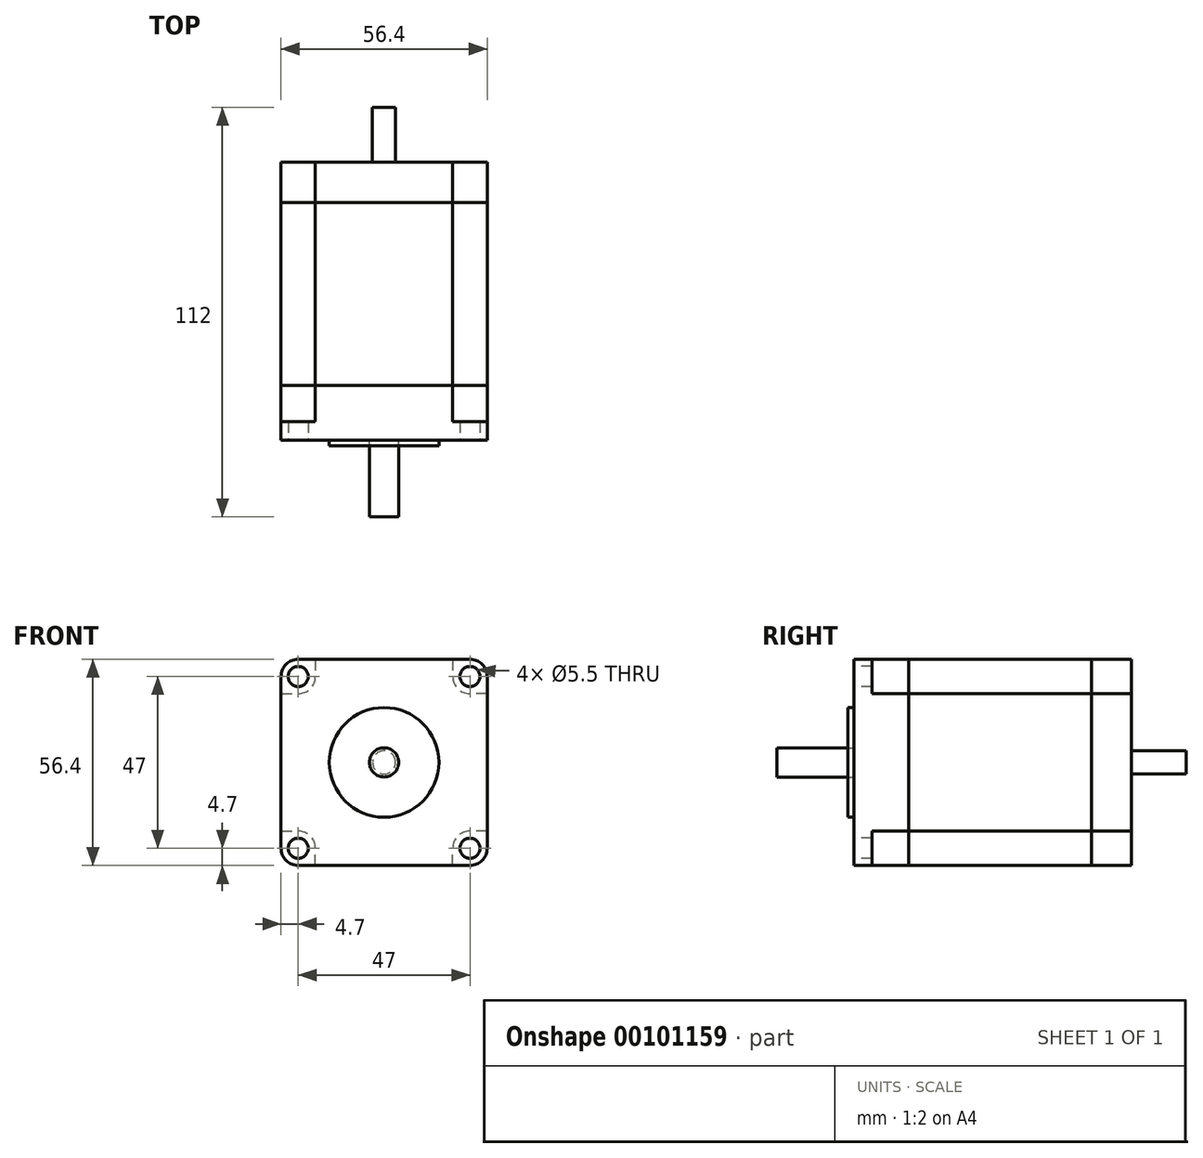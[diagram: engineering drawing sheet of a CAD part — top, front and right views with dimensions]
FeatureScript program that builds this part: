
annotation { "Feature Type Name" : "Feature", "Feature Type Description" : "" }
export const myFeature = defineFeature(function(context is Context, id is Id, definition is map)
    precondition{}
    {
        {
            var Q0;
            Q0=qCreatedBy(makeId("Front.planeOp"),FACE);
            var sketch = newSketch(context, id + "F0", { "sketchPlane" : qUnion([Q0])});
            skLineSegment(sketch, "E0.bottom", {"start": v(28.2, 28.2) * mm, "end": v(-28.2, 28.2) * mm});
            skLineSegment(sketch, "E0.top", {"start": v(28.2, -28.2) * mm, "end": v(-28.2, -28.2) * mm});
            skLineSegment(sketch, "E0.left", {"start": v(28.2, 28.2) * mm, "end": v(28.2, -28.2) * mm});
            skLineSegment(sketch, "E0.right", {"start": v(-28.2, 28.2) * mm, "end": v(-28.2, -28.2) * mm});
            skPoint(sketch, "E0.middle", {"position": v(0, 0) * mm});
            skSolve(sketch);
        }
        {
            var Q0;
            Q0=makeQuery(id+"F0.imprint","IMPRINT",FACE,{"disambiguationData":[TD([[makeQuery(id+"F0.imprint","IMPRINT",EDGE,{"derivedFrom":sQuery(id+"F0.wireOp",EDGE,"E0.bottom")}),1.0]])]});
            extrude(context, id + "F1", {"entities" : qUnion([Q0]), "oppositeDirection" : true, "depth" : 15 * mm});
        }
        {
            var Q0;
            Q0=makeQuery(id+"F1.opExtrude","CAP_FACE",FACE,{"disambiguationData":[OSD([sQuery(id+"F0.wireOp",EDGE,"E0.bottom"),sQuery(id+"F0.wireOp",EDGE,"E0.top"),sQuery(id+"F0.wireOp",EDGE,"E0.left"),sQuery(id+"F0.wireOp",EDGE,"E0.right")])],"isStart":true});
            var sketch = newSketch(context, id + "F2", { "sketchPlane" : qUnion([Q0])});
            skPoint(sketch, "E1", {"position": v(-23.5, 23.5) * mm});
            skPoint(sketch, "E2", {"position": v(23.5, 23.5) * mm});
            skPoint(sketch, "E3", {"position": v(23.5, -23.5) * mm});
            skPoint(sketch, "E4", {"position": v(-23.5, -23.5) * mm});
            skLineSegment(sketch, "E5", {"start": v(-23.5, 23.5) * mm, "end": v(-23.5, -23.5) * mm, "construction": true});
            skLineSegment(sketch, "E6", {"start": v(-23.5, -23.5) * mm, "end": v(23.5, -23.5) * mm, "construction": true});
            skLineSegment(sketch, "E7", {"start": v(23.5, -23.5) * mm, "end": v(23.5, 23.5) * mm, "construction": true});
            skLineSegment(sketch, "E8", {"start": v(-23.5, 23.5) * mm, "end": v(23.5, 23.5) * mm, "construction": true});
            skLineSegment(sketch, "E9", {"start": v(23.5, 23.5) * mm, "end": v(0, 0) * mm, "construction": true});
            skLineSegment(sketch, "E10", {"start": v(0, 0) * mm, "end": v(-23.5, -23.5) * mm, "construction": true});
            skLineSegment(sketch, "E11", {"start": v(23.5, -23.5) * mm, "end": v(0, 0) * mm, "construction": true});
            skLineSegment(sketch, "E12", {"start": v(-23.5, 23.5) * mm, "end": v(0, 0) * mm, "construction": true});
            skSolve(sketch);
        }
        {
            var Q0;
            Q0=sQuery(id+"F2.wireOp",VERTEX,"E4");
            var Q1;
            Q1=sQuery(id+"F2.wireOp",VERTEX,"E1");
            var Q2;
            Q2=sQuery(id+"F2.wireOp",VERTEX,"E2");
            var Q3;
            Q3=sQuery(id+"F2.wireOp",VERTEX,"E3");
            var Q4;
            Q4=makeQuery(id+"F1.opExtrude","SWEPT_BODY",BODY,{"disambiguationData":[OSD([sQuery(id+"F0.wireOp",EDGE,"E0.bottom"),sQuery(id+"F0.wireOp",EDGE,"E0.top"),sQuery(id+"F0.wireOp",EDGE,"E0.left"),sQuery(id+"F0.wireOp",EDGE,"E0.right")])]});
            hole(context, id + "F3", {"style" : HoleStyle.SIMPLE, "endStyle" : HoleEndStyle.THROUGH, "standardTappedOrClearance" : lookupTablePath({ "standard" : "ISO", "fit" : "Normal", "size" : "M5", "type" : "Clearance" }), "standardBlindInLast" : lookupTablePath({ "fit" : "Standard", "standard" : "ISO", "size" : "M5", "type" : "Clearance" }), "holeDiameter" : 5.5 * mm, "locations" : qUnion([Q0, Q1, Q2, Q3]), "scope" : qUnion([Q4]), "isTappedThrough" : true});
        }
        {
            var Q0;
            Q0=makeQuery(id+"F1.opExtrude","CAP_FACE",FACE,{"disambiguationData":[OSD([sQuery(id+"F0.wireOp",EDGE,"E0.bottom"),sQuery(id+"F0.wireOp",EDGE,"E0.top"),sQuery(id+"F0.wireOp",EDGE,"E0.left"),sQuery(id+"F0.wireOp",EDGE,"E0.right")])],"isStart":false});
            var sketch = newSketch(context, id + "F4", { "sketchPlane" : qUnion([Q0])});
            skLineSegment(sketch, "E13.bottom", {"start": v(28.2, 28.2) * mm, "end": v(18.8, 28.2) * mm});
            skLineSegment(sketch, "E13.top", {"start": v(28.2, 18.8) * mm, "end": v(23.5, 18.8) * mm});
            skLineSegment(sketch, "E13.left", {"start": v(28.2, 28.2) * mm, "end": v(28.2, 18.8) * mm});
            skLineSegment(sketch, "E13.right", {"start": v(18.8, 28.2) * mm, "end": v(18.8, 23.5) * mm});
            skLineSegment(sketch, "E14", {"start": v(23.5, 28.2) * mm, "end": v(23.5, 26.25) * mm, "construction": true});
            skLineSegment(sketch, "E15", {"start": v(23.5, 20.75) * mm, "end": v(23.5, 18.8) * mm, "construction": true});
            skLineSegment(sketch, "E16", {"start": v(28.2, 23.5) * mm, "end": v(26.25, 23.5) * mm, "construction": true});
            skLineSegment(sketch, "E17", {"start": v(18.8, 23.5) * mm, "end": v(20.75, 23.5) * mm, "construction": true});
            skPoint(sketch, "E18.center.orphan", {"position": v(23.5, 23.5) * mm});
            skPoint(sketch, "E19.visualSharp", {"position": v(18.8, 18.8) * mm});
            skArc(sketch, "E19.filletArc", {"start": v(18.8, 23.5) * mm, "mid": v(20.18, 20.18) * mm, "end": v(23.5, 18.8) * mm});
            skLineSegment(sketch, "E20", {"start": v(28.2, 0) * mm, "end": v(-28.2, 0) * mm, "construction": true});
            skLineSegment(sketch, "E21", {"start": v(0, 28.2) * mm, "end": v(0, -28.2) * mm, "construction": true});
            skLineSegment(sketch, "E22.MirrorCS", {"start": v(28.2, -18.8) * mm, "end": v(23.5, -18.8) * mm});
            skArc(sketch, "E23.MirrorCS", {"start": v(18.8, -23.5) * mm, "mid": v(20.18, -20.18) * mm, "end": v(23.5, -18.8) * mm});
            skLineSegment(sketch, "E24.MirrorCS", {"start": v(18.8, -28.2) * mm, "end": v(18.8, -23.5) * mm});
            skLineSegment(sketch, "E25.MirrorCS", {"start": v(28.2, -28.2) * mm, "end": v(18.8, -28.2) * mm});
            skLineSegment(sketch, "E26.MirrorCS", {"start": v(28.2, -28.2) * mm, "end": v(28.2, -18.8) * mm});
            skLineSegment(sketch, "E27.MirrorCS", {"start": v(-18.8, 28.2) * mm, "end": v(-18.8, 23.5) * mm});
            skArc(sketch, "E28.MirrorCS", {"start": v(-18.8, 23.5) * mm, "mid": v(-20.18, 20.18) * mm, "end": v(-23.5, 18.8) * mm});
            skLineSegment(sketch, "E29.MirrorCS", {"start": v(-28.2, 18.8) * mm, "end": v(-23.5, 18.8) * mm});
            skLineSegment(sketch, "E30.MirrorCS", {"start": v(-28.2, 28.2) * mm, "end": v(-28.2, 18.8) * mm});
            skLineSegment(sketch, "E31.MirrorCS", {"start": v(-28.2, 28.2) * mm, "end": v(-18.8, 28.2) * mm});
            skLineSegment(sketch, "E32.MirrorCS", {"start": v(-28.2, -28.2) * mm, "end": v(-28.2, -18.8) * mm});
            skLineSegment(sketch, "E33.MirrorCS", {"start": v(-28.2, -18.8) * mm, "end": v(-23.5, -18.8) * mm});
            skArc(sketch, "E34.MirrorCS", {"start": v(-18.8, -23.5) * mm, "mid": v(-20.18, -20.18) * mm, "end": v(-23.5, -18.8) * mm});
            skLineSegment(sketch, "E35.MirrorCS", {"start": v(-18.8, -28.2) * mm, "end": v(-18.8, -23.5) * mm});
            skLineSegment(sketch, "E36.MirrorCS", {"start": v(-28.2, -28.2) * mm, "end": v(-18.8, -28.2) * mm});
            skSolve(sketch);
        }
        {
            var Q0;
            Q0 = qSketchRegion(id + "F4", true);
            extrude(context, id + "F5", {"entities" : qUnion([Q0]), "operationType" : NewBodyOperationType.REMOVE, "oppositeDirection" : true, "depth" : 10 * mm});
        }
        {
            var Q0;
            Q0=makeQuery(id+"F5.boolean.opBoolean","COPY",FACE,{"derivedFrom":makeQuery(id+"F5.opExtrude","CAP_FACE",FACE,{"disambiguationData":[OSD([sQuery(id+"F4.wireOp",EDGE,"E13.bottom"),sQuery(id+"F4.wireOp",EDGE,"E13.top"),sQuery(id+"F4.wireOp",EDGE,"E13.left"),sQuery(id+"F4.wireOp",EDGE,"E13.right"),sQuery(id+"F4.wireOp",EDGE,"E19.filletArc")])],"isStart":false})});
            var sketch = newSketch(context, id + "F6", { "sketchPlane" : qUnion([Q0])});
            skLineSegment(sketch, "E37", {"start": v(28.2, 23.5) * mm, "end": v(28.2, 28.2) * mm});
            skLineSegment(sketch, "E38", {"start": v(28.2, 28.2) * mm, "end": v(23.5, 28.2) * mm});
            skArc(sketch, "E39", {"start": v(23.5, 28.2) * mm, "mid": v(26.82, 26.82) * mm, "end": v(28.2, 23.5) * mm});
            skLineSegment(sketch, "E40.MirrorCS", {"start": v(28.2, -28.2) * mm, "end": v(23.5, -28.2) * mm});
            skArc(sketch, "E41.MirrorCS", {"start": v(23.5, -28.2) * mm, "mid": v(26.82, -26.82) * mm, "end": v(28.2, -23.5) * mm});
            skLineSegment(sketch, "E42.MirrorCS", {"start": v(28.2, -23.5) * mm, "end": v(28.2, -28.2) * mm});
            skLineSegment(sketch, "E43.MirrorCS", {"start": v(-28.2, 28.2) * mm, "end": v(-23.5, 28.2) * mm});
            skArc(sketch, "E44.MirrorCS", {"start": v(-23.5, 28.2) * mm, "mid": v(-26.82, 26.82) * mm, "end": v(-28.2, 23.5) * mm});
            skLineSegment(sketch, "E45.MirrorCS", {"start": v(-28.2, 23.5) * mm, "end": v(-28.2, 28.2) * mm});
            skArc(sketch, "E46.MirrorCS", {"start": v(-23.5, -28.2) * mm, "mid": v(-26.82, -26.82) * mm, "end": v(-28.2, -23.5) * mm});
            skLineSegment(sketch, "E47.MirrorCS", {"start": v(-28.2, -23.5) * mm, "end": v(-28.2, -28.2) * mm});
            skLineSegment(sketch, "E48.MirrorCS", {"start": v(-28.2, -28.2) * mm, "end": v(-23.5, -28.2) * mm});
            skSolve(sketch);
        }
        {
            var Q0;
            Q0 = qSketchRegion(id + "F6", true);
            extrude(context, id + "F7", {"entities" : qUnion([Q0]), "operationType" : NewBodyOperationType.REMOVE, "endBound" : BoundingType.THROUGH_ALL, "oppositeDirection" : true, "depth" : 25 * mm});
        }
        {
            var Q0;
            Q0=makeQuery(id+"F1.opExtrude","CAP_FACE",FACE,{"disambiguationData":[OSD([sQuery(id+"F0.wireOp",EDGE,"E0.bottom"),sQuery(id+"F0.wireOp",EDGE,"E0.top"),sQuery(id+"F0.wireOp",EDGE,"E0.left"),sQuery(id+"F0.wireOp",EDGE,"E0.right")])],"isStart":false});
            extrude(context, id + "F8", {"entities" : qUnion([Q0]), "depth" : 50 * mm});
        }
        {
            var Q0;
            Q0=makeQuery(id+"F8.opExtrude","CAP_FACE",FACE,{"disambiguationData":[OSD([sQuery(id+"F0.wireOp",EDGE,"E0.bottom"),sQuery(id+"F0.wireOp",EDGE,"E0.top"),sQuery(id+"F0.wireOp",EDGE,"E0.left"),sQuery(id+"F0.wireOp",EDGE,"E0.right")])],"isStart":false});
            extrude(context, id + "F9", {"entities" : qUnion([Q0]), "depth" : 11 * mm});
        }
        {
            var Q0;
            Q0=makeQuery(id+"F1.opExtrude","CAP_FACE",FACE,{"disambiguationData":[OSD([sQuery(id+"F0.wireOp",EDGE,"E0.bottom"),sQuery(id+"F0.wireOp",EDGE,"E0.top"),sQuery(id+"F0.wireOp",EDGE,"E0.left"),sQuery(id+"F0.wireOp",EDGE,"E0.right")])],"isStart":true});
            var sketch = newSketch(context, id + "F10", { "sketchPlane" : qUnion([Q0])});
            skCircle(sketch, "E49", {"center": v(0, 0) * mm, "radius": 15 * mm});
            skSolve(sketch);
        }
        {
            var Q0;
            Q0 = qSketchRegion(id + "F10", true);
            extrude(context, id + "F11", {"entities" : qUnion([Q0]), "operationType" : NewBodyOperationType.ADD, "depth" : 1.6 * mm});
        }
        {
            var Q0;
            Q0=makeQuery(id+"F1.opExtrude","CAP_FACE",FACE,{"disambiguationData":[OSD([sQuery(id+"F0.wireOp",EDGE,"E0.bottom"),sQuery(id+"F0.wireOp",EDGE,"E0.top"),sQuery(id+"F0.wireOp",EDGE,"E0.left"),sQuery(id+"F0.wireOp",EDGE,"E0.right")])],"isStart":true});
            var sketch = newSketch(context, id + "F12", { "sketchPlane" : qUnion([Q0])});
            skCircle(sketch, "E50", {"center": v(0, 0) * mm, "radius": 4 * mm});
            skSolve(sketch);
        }
        {
            var Q0;
            Q0 = qSketchRegion(id + "F12", true);
            extrude(context, id + "F13", {"entities" : qUnion([Q0]), "depth" : 21 * mm});
        }
        {
            var Q0;
            Q0=makeQuery(id+"F9.opExtrude","CAP_FACE",FACE,{"disambiguationData":[OSD([sQuery(id+"F0.wireOp",EDGE,"E0.bottom"),sQuery(id+"F0.wireOp",EDGE,"E0.top"),sQuery(id+"F0.wireOp",EDGE,"E0.left"),sQuery(id+"F0.wireOp",EDGE,"E0.right")])],"isStart":false});
            var sketch = newSketch(context, id + "F14", { "sketchPlane" : qUnion([Q0])});
            skCircle(sketch, "E51", {"center": v(0, 0) * mm, "radius": 3.18 * mm});
            skSolve(sketch);
        }
        {
            var Q0;
            Q0 = qSketchRegion(id + "F14", true);
            extrude(context, id + "F15", {"entities" : qUnion([Q0]), "depth" : 15 * mm});
        }
    });
